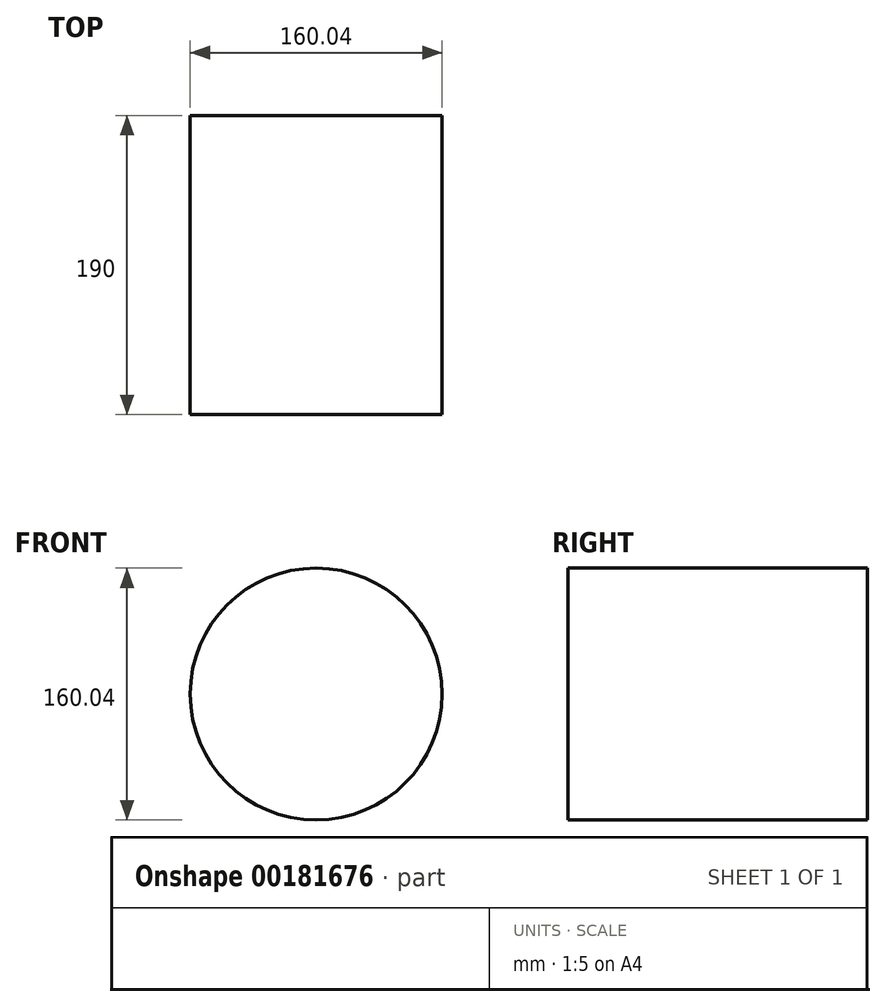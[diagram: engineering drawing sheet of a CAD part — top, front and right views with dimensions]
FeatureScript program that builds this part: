
annotation { "Feature Type Name" : "Feature", "Feature Type Description" : "" }
export const myFeature = defineFeature(function(context is Context, id is Id, definition is map)
    precondition{}
    {
        {
            var Q0;
            Q0=qCreatedBy(makeId("Front.planeOp"),FACE);
            var sketch = newSketch(context, id + "F0", { "sketchPlane" : qUnion([Q0])});
            skCircle(sketch, "E0", {"center": v(0, 0) * mm, "radius": 80.02 * mm});
            skSolve(sketch);
        }
        {
            var Q0;
            Q0 = qSketchRegion(id + "F0", true);
            extrude(context, id + "F1", {"entities" : qUnion([Q0]), "depth" : 190 * mm});
        }
    });
